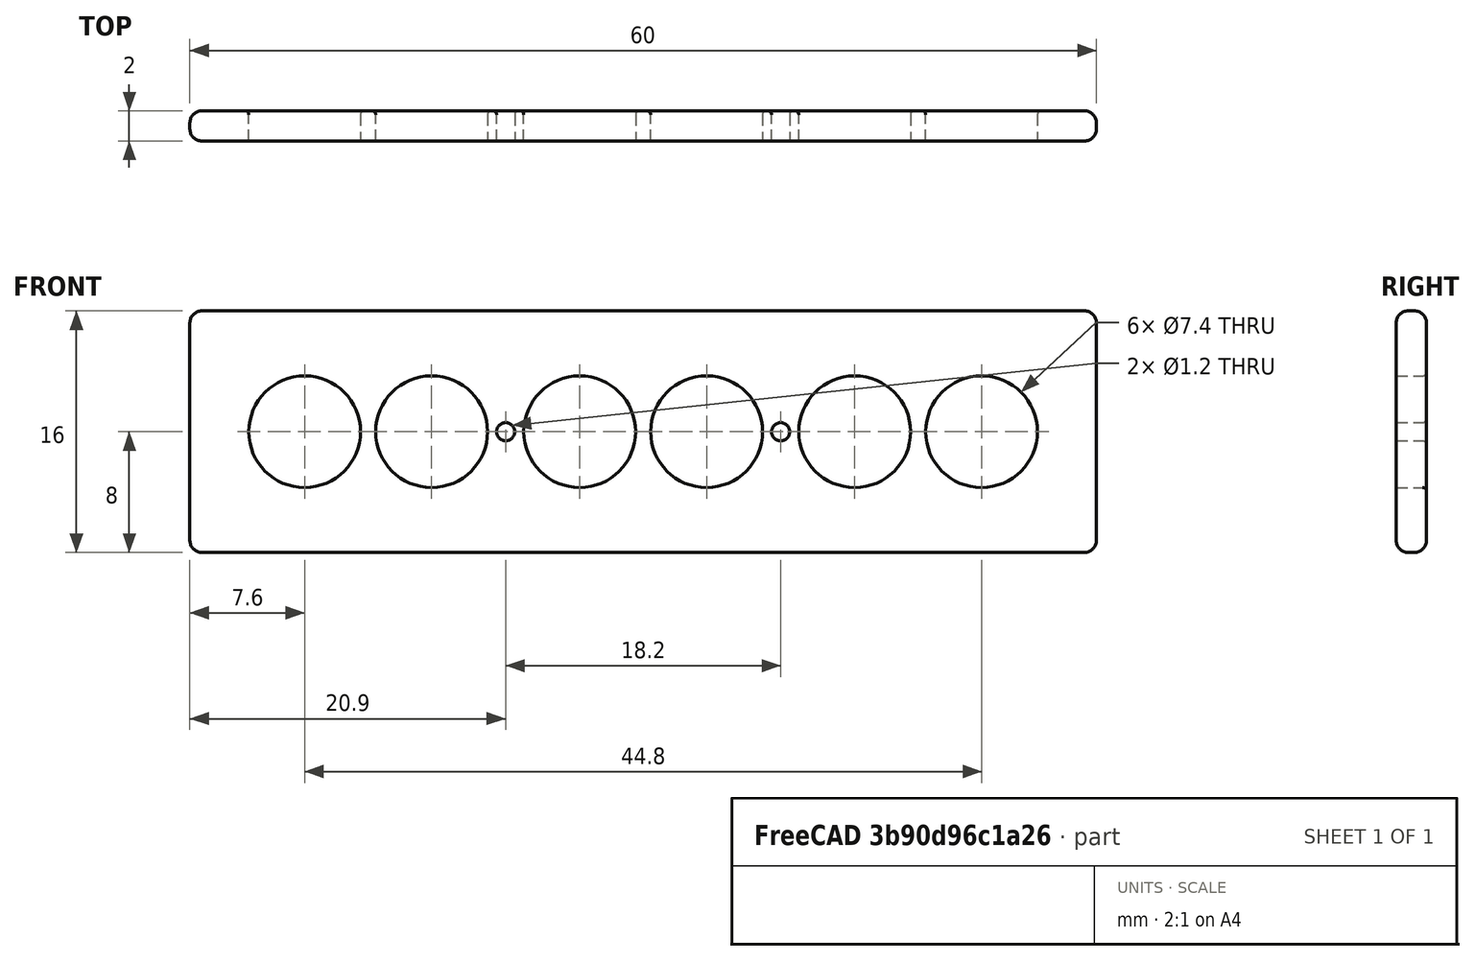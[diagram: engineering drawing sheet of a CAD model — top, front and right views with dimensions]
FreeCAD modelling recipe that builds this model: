
FCSTD DOCUMENT  (FreeCAD 0.16R6712 (Git))
Label: top6
License: All rights reserved
LicenseURL: http://en.wikipedia.org/wiki/All_rights_reserved
objects: Sketcher::SketchObject×3, PartDesign::Fillet×2, PartDesign::Pad×1, PartDesign::Pocket×1, Mesh::Feature×1
note: 9 computed .brp shape members not serialized (recipe doc carries the construction recipe); baked Part::Feature solids carry a one-line shape summary decoded from their .brp

FEATURE [Sketcher::SketchObject] Sketch
  Placement = pos=(0,0,0) rot=(-1,0,0;4.71239rad)
FEATURE [Sketcher::SketchObject] Sketch001
  Placement = pos=(0,-3,0) rot=(1,0,0;1.5708rad)
  sketch-geometry (4):
    g0: LineSegment StartX=-30 StartY=8 StartZ=0 EndX=30 EndY=8 EndZ=0
    g1: LineSegment StartX=30 StartY=8 StartZ=0 EndX=30 EndY=-8 EndZ=0
    g2: LineSegment StartX=30 StartY=-8 StartZ=0 EndX=-30 EndY=-8 EndZ=0
    g3: LineSegment StartX=-30 StartY=-8 StartZ=0 EndX=-30 EndY=8 EndZ=0
  constraints (12):
    c: Coincident(g0,g1)
    c: Coincident(g1,g2)
    c: Coincident(g2,g3)
    c: Coincident(g3,g0)
    c: Horizontal(g0)
    c: Horizontal(g2)
    c: Vertical(g1)
    c: Vertical(g3)
    c: Symmetric(g0,g0,g-2)
    c: Symmetric(g1,g0,g-1)
    c: DistanceX(g-2,g0) = 30
    c: DistanceY(g-1,g0) = 8
FEATURE [PartDesign::Pad] Pad
  Length = 2
  Length2 = 100
  Placement = pos=(0,-3,0) rot=(1,0,0;1.5708rad)
  Sketch = -> Sketch001
  Type = 0
FEATURE [PartDesign::Fillet] Fillet
  Base = -> Pad [Edge4,Edge7,Edge10,Edge12,Edge5,Edge8,Edge9,Edge1,Edge11,Edge3,Edge6,Edge2]
  Placement = pos=(0,-3,0) rot=(1,0,0;1.5708rad)
  Radius = 0.8
FEATURE [Sketcher::SketchObject] Sketch002
  Placement = pos=(0,-3,0) rot=(-1,0,0;1.5708rad)
  Support = -> Fillet [Face13]
  sketch-geometry (8):
    g0: Circle CenterX=4.2 CenterY=0 CenterZ=0 NormalX=0 NormalY=0 NormalZ=1 Radius=3.7
    g1: Circle CenterX=-4.2 CenterY=0 CenterZ=0 NormalX=0 NormalY=0 NormalZ=1 Radius=3.7
    g2: Circle CenterX=-14 CenterY=0 CenterZ=0 NormalX=0 NormalY=0 NormalZ=1 Radius=3.7
    g3: Circle CenterX=-22.4 CenterY=0 CenterZ=0 NormalX=0 NormalY=0 NormalZ=1 Radius=3.7
    g4: Circle CenterX=14 CenterY=0 CenterZ=0 NormalX=0 NormalY=0 NormalZ=1 Radius=3.7
    g5: Circle CenterX=22.4 CenterY=0 CenterZ=0 NormalX=0 NormalY=0 NormalZ=1 Radius=3.7
    g6: Circle CenterX=-9.1 CenterY=0 CenterZ=0 NormalX=0 NormalY=0 NormalZ=1 Radius=0.6
    g7: Circle CenterX=9.1 CenterY=0 CenterZ=0 NormalX=0 NormalY=0 NormalZ=1 Radius=0.6
  constraints (24):
    c: PointOnObject(g0,g-1)
    c: Radius(g5) = 3.7
    c: Equal(g5,g4)
    c: Equal(g4,g0)
    c: Equal(g0,g1)
    c: Equal(g1,g2)
    c: Equal(g2,g3)
    c: PointOnObject(g3,g-1)
    c: PointOnObject(g2,g-1)
    c: PointOnObject(g1,g-1)
    c: PointOnObject(g4,g-1)
    c: PointOnObject(g5,g-1)
    c: DistanceX(g-2,g0) = 4.2
    c: DistanceX(g-2,g4) = 14
    c: Distance(g4,g5) = 8.4
    c: Symmetric(g1,g0,g-2)
    c: Symmetric(g2,g4,g-2)
    c: Symmetric(g3,g5,g-2)
    c: PointOnObject(g7,g-1)
    c: PointOnObject(g6,g-1)
    c: Symmetric(g6,g7,g-2)
    c: Radius(g6) = 0.6
    c: Equal(g6,g7)
    c: DistanceX(g-2,g6) = -9.1
FEATURE [PartDesign::Pocket] Pocket
  Length = 5
  Placement = pos=(0,-3,0) rot=(1,0,0;1.5708rad)
  Sketch = -> Sketch002
  Type = 0
FEATURE [PartDesign::Fillet] Fillet001
  Base = -> Pocket [Edge45,Edge46,Edge47,Edge48,Edge49,Edge50,Edge51,Edge52]
  Placement = pos=(0,-3,0) rot=(1,0,0;1.5708rad)
  Radius = 0.25
FEATURE [Mesh::Feature] Mesh  label="Fillet001 (Meshed)"
